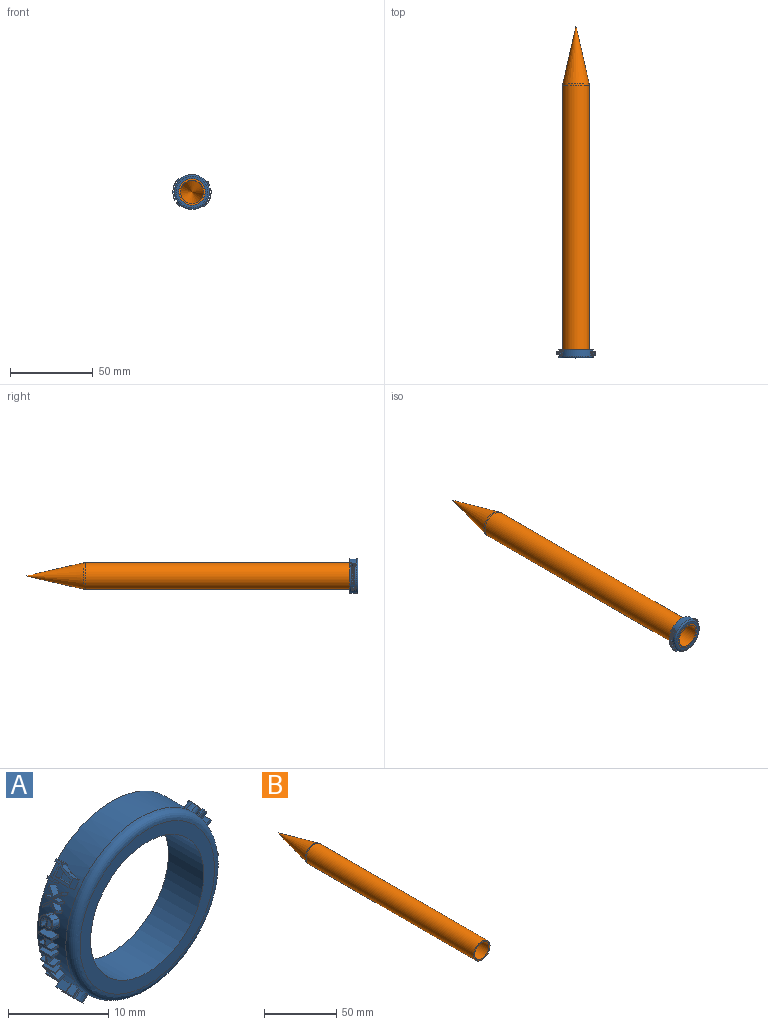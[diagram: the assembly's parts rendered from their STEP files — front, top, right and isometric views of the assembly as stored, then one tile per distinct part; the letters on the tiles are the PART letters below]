
ASSEMBLY  parts=2 mates=1
PART A: 312 faces, bbox 23x5x21 mm
  f0: plane 2.34x0.74mm, normal (0.74,0,0.67), area 2.3mm2, adj f1,f9,f10,f32
  f1: plane 0.93x0.87mm, normal (0,-1,0), area 0.3mm2, adj f0,f2,f10,f32
  f2: plane 2.36x0.74mm, normal (-0.74,0,-0.67), area 2.4mm2, adj f1,f3,f10,f32
  f3: extruded ~0.8x0.73mm, area 0.3mm2, adj f2,f4,f10,f32
  f4: extruded ~0.91x0.86mm, area 0.3mm2, adj f3,f5,f10,f32
  f5: extruded ~0.91x0.86mm, area 0.2mm2, adj f4,f6,f10,f32
  f6: plane 0.74x0.67mm, normal (-0.74,0,-0.67), area 0.2mm2, adj f5,f7,f10,f32
  f7: extruded ~0.91x0.86mm, area 0.2mm2, adj f6,f8,f10,f32
  f8: extruded ~1.05x1.01mm, area 0.5mm2, adj f7,f9,f10,f32
  f9: extruded ~0.85x0.79mm, area 0.5mm2, adj f0,f8,f10,f32
  f10: cylinder r=11.5mm len=2.98mm, axis (0,1,0), area 0.9mm2, adj f0,f1,f2,f3,f4,f5,f6,f7
  f11: extruded ~0.96x0.85mm, area 0.3mm2, adj f12,f24,f30,f32
  f12: extruded ~0.97x0.87mm, area 0.3mm2, adj f11,f13,f30,f32
  f13: extruded ~1.18x1.12mm, area 0.7mm2, adj f12,f14,f30,f32
  f14: extruded ~0.93x0.82mm, area 0.7mm2, adj f13,f15,f30,f32
  f15: extruded ~0.92x0.8mm, area 0.7mm2, adj f14,f16,f30,f32
  f16: extruded ~1.14x1.08mm, area 0.6mm2, adj f15,f17,f30,f32
  f17: extruded ~1.12x1.05mm, area 0.6mm2, adj f16,f18,f30,f32
  f18: extruded ~0.91x0.79mm, area 0.6mm2, adj f17,f19,f30,f32
  f19: plane 0.78x0.63mm, normal (0.63,0,0.78), area 0.2mm2, adj f18,f20,f30,f32
  f20: plane 1.59x1.53mm, normal (0,1,0), area 1.2mm2, adj f19,f21,f30,f32
  f21: extruded ~0.88x0.76mm, area 0.5mm2, adj f20,f22,f30,f32
  f22: extruded ~1.05x0.96mm, area 0.5mm2, adj f21,f23,f30,f32
  f23: extruded ~1.15x1.08mm, area 0.6mm2, adj f22,f24,f30,f32
  f24: plane 0.78x0.63mm, normal (0.63,0,0.78), area 0.2mm2, adj f11,f23,f30,f32
  f25: plane 1.36x1.35mm, normal (0,-1,0), area 0.9mm2, adj f26,f29,f30,f31
  f26: extruded ~0.88x0.75mm, area 0.4mm2, adj f25,f27,f30,f31
  f27: extruded ~0.99x0.9mm, area 0.4mm2, adj f26,f28,f30,f31
  f28: extruded ~0.98x0.88mm, area 0.4mm2, adj f27,f29,f30,f31
  f29: extruded ~0.85x0.72mm, area 0.4mm2, adj f25,f28,f30,f31
  f30: cylinder r=11.5mm len=1.83mm, axis (0,1,0), area 1.2mm2, adj f11,f12,f13,f14,f15,f16,f17,f18
  f31: cylinder r=10.5mm len=0.72mm, axis (0,1,0), area 0.4mm2, adj f25,f26,f27,f28,f29
  f32: cylinder r=10.5mm len=21mm, axis (0,1,0), area 238.7mm2, adj f0,f1,f2,f3,f4,f5,f6,f7
  f33: plane 1.21x0.88mm, normal (0.48,0,0.87), area 1.2mm2, adj f32,f34,f51,f60
  f34: plane 0.96x0.66mm, normal (0,1,0), area 0.2mm2, adj f32,f33,f35,f60
  f35: plane 0.9x0.53mm, normal (-0.47,0.21,-0.86), area 0.3mm2, adj f32,f34,f36,f60
  f36: plane 0.88x0.5mm, normal (0,1,0), area 0mm2, adj f32,f35,f37,f60
  f37: extruded ~1.01x0.72mm, area 0.4mm2, adj f32,f36,f38,f60
  f38: extruded ~1.03x0.77mm, area 0.3mm2, adj f32,f37,f39,f60
  f39: extruded ~1.09x0.85mm, area 0.4mm2, adj f32,f38,f40,f60
  f40: extruded ~0.96x0.62mm, area 0.4mm2, adj f32,f39,f41,f60
  f41: extruded ~1.31x1.25mm, area 1.2mm2, adj f32,f40,f42,f60
  f42: plane 1.01x0.75mm, normal (-0.02,-1,-0.03), area 0.3mm2, adj f32,f41,f43,f60
  f43: plane 0.88x0.49mm, normal (-0.48,0,-0.87), area 0.1mm2, adj f32,f42,f44,f60
  f44: extruded ~0.92x0.56mm, area 0.3mm2, adj f32,f43,f45,f60
  f45: extruded ~1.02x0.74mm, area 0.3mm2, adj f32,f44,f46,f60
  f46: extruded ~1.13x0.93mm, area 0.5mm2, adj f32,f45,f47,f60
  f47: plane 0.92x0.56mm, normal (-0.45,0.37,-0.81), area 0.2mm2, adj f32,f46,f48,f60
  f48: extruded ~1.02x0.74mm, area 0.3mm2, adj f32,f47,f49,f60
  f49: extruded ~1.03x0.76mm, area 0.3mm2, adj f32,f48,f50,f60
  f50: extruded ~1.11x0.9mm, area 0.5mm2, adj f32,f49,f51,f60
  f51: extruded ~0.96x0.62mm, area 0.5mm2, adj f32,f33,f50,f60
  f52: extruded ~0.95x0.61mm, area 0.3mm2, adj f53,f59,f60,f61
  f53: extruded ~1.1x0.89mm, area 0.5mm2, adj f52,f54,f60,f61
  f54: plane 1x0.72mm, normal (0.02,1,0.04), area 0.3mm2, adj f53,f55,f60,f61
  f55: plane 0.88x0.49mm, normal (-0.48,0,-0.87), area 0.2mm2, adj f54,f56,f60,f61
  f56: extruded ~0.95x0.61mm, area 0.4mm2, adj f55,f57,f60,f61
  f57: extruded ~1.07x0.83mm, area 0.4mm2, adj f56,f58,f60,f61
  f58: extruded ~1x0.7mm, area 0.3mm2, adj f57,f59,f60,f61
  f59: extruded ~0.92x0.56mm, area 0.2mm2, adj f52,f58,f60,f61
  f60: cylinder r=11.5mm len=1.83mm, axis (0,1,0), area 1.2mm2, adj f33,f34,f35,f36,f37,f38,f39,f40
  f61: cylinder r=10.5mm len=0.76mm, axis (0,1,0), area 0.4mm2, adj f52,f53,f54,f55,f56,f57,f58,f59
  f62: extruded ~1.01x0.49mm, area 0.5mm2, adj f32,f63,f78,f79
  f63: extruded ~1.12x0.78mm, area 0.5mm2, adj f32,f62,f64,f79
  f64: extruded ~1.05x0.63mm, area 0.3mm2, adj f32,f63,f65,f79
  f65: extruded ~1.03x0.54mm, area 0.3mm2, adj f32,f64,f66,f79
  f66: plane 0.95x0.33mm, normal (0,-1,0), area 0mm2, adj f32,f65,f67,f79
  f67: plane 0.96x0.36mm, normal (0.32,-0.18,0.93), area 0.2mm2, adj f32,f66,f68,f79
  f68: plane 1.03x0.52mm, normal (0,-1,0), area 0.2mm2, adj f32,f67,f69,f79
  f69: plane 1.77x0.95mm, normal (-0.32,0,-0.95), area 1.8mm2, adj f32,f68,f70,f79
  f70: plane 1.05x0.57mm, normal (0,1,0), area 0.3mm2, adj f32,f69,f71,f79
  f71: plane 0.95x0.93mm, normal (0.32,0,0.95), area 0.9mm2, adj f32,f70,f72,f79
  f72: extruded ~0.99x0.5mm, area 0.5mm2, adj f32,f71,f73,f79
  f73: extruded ~1.08x0.71mm, area 0.4mm2, adj f32,f72,f74,f79
  f74: extruded ~1.05x0.62mm, area 0.3mm2, adj f32,f73,f75,f79
  f75: extruded ~0.98x0.42mm, area 0.3mm2, adj f32,f74,f76,f79
  f76: plane 1.14x0.95mm, normal (-0.32,0,-0.95), area 1.1mm2, adj f32,f75,f77,f79
  f77: plane 1.02x0.58mm, normal (0,1,0), area 0.3mm2, adj f32,f76,f78,f79
  f78: plane 1.15x0.95mm, normal (0.32,0,0.95), area 1.2mm2, adj f32,f62,f77,f79
  f79: cylinder r=11.5mm len=1.8mm, axis (0,1,0), area 1.1mm2, adj f62,f63,f64,f65,f66,f67,f68,f69
  f80: extruded ~1.03x0.49mm, area 0.5mm2, adj f32,f81,f96,f97
  f81: extruded ~1.07x0.62mm, area 0.5mm2, adj f32,f80,f82,f97
  f82: extruded ~1.04x0.47mm, area 0.3mm2, adj f32,f81,f83,f97
  f83: extruded ~1.03x0.37mm, area 0.3mm2, adj f32,f82,f84,f97
  f84: plane 0.99x0.15mm, normal (0,-1,0), area 0mm2, adj f32,f83,f85,f97
  f85: plane 1x0.24mm, normal (0.14,-0.18,0.97), area 0.2mm2, adj f32,f84,f86,f97
  f86: plane 1.03x0.35mm, normal (0,-1,0), area 0.2mm2, adj f32,f85,f87,f97
  f87: plane 1.77x0.99mm, normal (-0.14,0,-0.99), area 1.8mm2, adj f32,f86,f88,f97
  f88: plane 1.04x0.4mm, normal (0,1,0), area 0.3mm2, adj f32,f87,f89,f97
  f89: plane 0.99x0.93mm, normal (0.14,0,0.99), area 0.9mm2, adj f32,f88,f90,f97
  f90: extruded ~1.01x0.5mm, area 0.5mm2, adj f32,f89,f91,f97
  f91: extruded ~1.05x0.54mm, area 0.4mm2, adj f32,f90,f92,f97
  f92: extruded ~1.04x0.45mm, area 0.3mm2, adj f32,f91,f93,f97
  f93: extruded ~1.01x0.32mm, area 0.3mm2, adj f32,f92,f94,f97
  f94: plane 1.14x0.99mm, normal (-0.14,0,-0.99), area 1.1mm2, adj f32,f93,f95,f97
  f95: plane 1.01x0.41mm, normal (0,1,0), area 0.3mm2, adj f32,f94,f96,f97
  f96: plane 1.15x0.99mm, normal (0.14,0,0.99), area 1.2mm2, adj f32,f80,f95,f97
  f97: cylinder r=11.5mm len=1.8mm, axis (0,1,0), area 1.1mm2, adj f80,f81,f82,f83,f84,f85,f86,f87
  f98: plane 1.77x1mm, normal (-0.01,0,-1), area 1.8mm2, adj f32,f99,f101,f102
  f99: plane 1x0.28mm, normal (0,1,0), area 0.3mm2, adj f32,f98,f100,f102
  f100: plane 1.77x1mm, normal (0.01,0,1), area 1.8mm2, adj f32,f99,f101,f102
  f101: plane 1x0.28mm, normal (0,-1,0), area 0.3mm2, adj f32,f98,f100,f102
  f102: cylinder r=11.5mm len=1.77mm, axis (0,1,0), area 0.5mm2, adj f98,f99,f100,f101
  f103: extruded ~1x0.12mm, area 0.1mm2, adj f32,f104,f110,f111
  f104: extruded ~1x0.13mm, area 0.1mm2, adj f32,f103,f105,f111
  f105: extruded ~1x0.13mm, area 0.1mm2, adj f32,f104,f106,f111
  f106: extruded ~1x0.12mm, area 0.1mm2, adj f32,f105,f107,f111
  f107: extruded ~1x0.12mm, area 0.1mm2, adj f32,f106,f108,f111
  f108: extruded ~1x0.13mm, area 0.1mm2, adj f32,f107,f109,f111
  f109: extruded ~1x0.13mm, area 0.1mm2, adj f32,f108,f110,f111
  f110: extruded ~1x0.12mm, area 0.1mm2, adj f32,f103,f109,f111
  f111: cylinder r=11.5mm len=0.36mm, axis (0,1,0), area 0.1mm2, adj f103,f104,f105,f106,f107,f108,f109,f110
  f112: extruded ~1.04x0.39mm, area 0.3mm2, adj f32,f113,f125,f131
  f113: extruded ~1.04x0.43mm, area 0.3mm2, adj f32,f112,f114,f131
  f114: extruded ~1.08x0.74mm, area 0.7mm2, adj f32,f113,f115,f131
  f115: extruded ~1.04x0.66mm, area 0.7mm2, adj f32,f114,f116,f131
  f116: extruded ~1.03x0.68mm, area 0.7mm2, adj f32,f115,f117,f131
  f117: extruded ~1.08x0.68mm, area 0.6mm2, adj f32,f116,f118,f131
  f118: extruded ~1.07x0.64mm, area 0.6mm2, adj f32,f117,f119,f131
  f119: extruded ~1.03x0.58mm, area 0.6mm2, adj f32,f118,f120,f131
  f120: plane 1x0.17mm, normal (-0.12,0,0.99), area 0.2mm2, adj f32,f119,f121,f131
  f121: plane 1.33x1.16mm, normal (0,1,0), area 1.2mm2, adj f32,f120,f122,f131
  f122: extruded ~1.02x0.47mm, area 0.5mm2, adj f32,f121,f123,f131
  f123: extruded ~1.05x0.54mm, area 0.5mm2, adj f32,f122,f124,f131
  f124: extruded ~1.08x0.68mm, area 0.6mm2, adj f32,f123,f125,f131
  f125: plane 0.99x0.24mm, normal (-0.12,0,0.99), area 0.2mm2, adj f32,f112,f124,f131
  f126: plane 1.1x1.04mm, normal (0,-1,0), area 0.9mm2, adj f127,f130,f131,f132
  f127: extruded ~1.02x0.38mm, area 0.4mm2, adj f126,f128,f131,f132
  f128: extruded ~1.04x0.46mm, area 0.4mm2, adj f127,f129,f131,f132
  f129: extruded ~1.04x0.44mm, area 0.4mm2, adj f128,f130,f131,f132
  f130: extruded ~1.01x0.39mm, area 0.4mm2, adj f126,f129,f131,f132
  f131: cylinder r=11.5mm len=1.83mm, axis (0,1,0), area 1.2mm2, adj f112,f113,f114,f115,f116,f117,f118,f119
  f132: cylinder r=10.5mm len=0.92mm, axis (0,1,0), area 0.4mm2, adj f126,f127,f128,f129,f130
  f133: plane 1.16x0.96mm, normal (0.23,-0.79,-0.57), area 0.8mm2, adj f32,f134,f141,f142
  f134: plane 0.98x0.51mm, normal (0.3,0.61,-0.73), area 0.2mm2, adj f32,f133,f135,f142
  f135: extruded ~1.07x0.73mm, area 0.5mm2, adj f32,f134,f136,f142
  f136: extruded ~0.96x0.45mm, area 0.1mm2, adj f32,f135,f137,f142
  f137: extruded ~0.93x0.4mm, area 0.4mm2, adj f32,f136,f138,f142
  f138: plane 1.68x0.93mm, normal (0.38,0,-0.93), area 1.7mm2, adj f32,f137,f139,f142
  f139: plane 1.03x0.62mm, normal (0,1,0), area 0.3mm2, adj f32,f138,f140,f142
  f140: plane 2.36x0.93mm, normal (-0.38,0,0.93), area 2.4mm2, adj f32,f139,f141,f142
  f141: plane 1.02x0.58mm, normal (0,-1,0), area 0.2mm2, adj f32,f133,f140,f142
  f142: cylinder r=11.5mm len=2.36mm, axis (0,1,0), area 0.8mm2, adj f133,f134,f135,f136,f137,f138,f139,f140
  f143: extruded ~1.17x1.02mm, area 0.7mm2, adj f32,f144,f157,f168
  f144: extruded ~0.98x0.77mm, area 0.8mm2, adj f32,f143,f145,f168
  f145: extruded ~1.04x1.01mm, area 1.1mm2, adj f32,f144,f146,f168
  f146: extruded ~1.28x1.21mm, area 0.9mm2, adj f32,f145,f147,f168
  f147: extruded ~1.02x0.77mm, area 0.3mm2, adj f32,f146,f148,f168
  f148: plane 0.86x0.52mm, normal (-0.52,0,0.86), area 0.2mm2, adj f32,f147,f149,f168
  f149: extruded ~1.01x0.77mm, area 0.3mm2, adj f32,f148,f150,f168
  f150: extruded ~1.16x1.01mm, area 0.6mm2, adj f32,f149,f151,f168
  f151: extruded ~0.98x0.74mm, area 0.8mm2, adj f32,f150,f152,f168
  f152: plane 0.87x0.53mm, normal (0,-1,0), area 0mm2, adj f32,f151,f153,f168
  f153: extruded ~1.16x1mm, area 0.7mm2, adj f32,f152,f154,f168
  f154: extruded ~1.13x0.95mm, area 0.6mm2, adj f32,f153,f155,f168
  f155: extruded ~0.96x0.68mm, area 0.6mm2, adj f32,f154,f156,f168
  f156: extruded ~0.97x0.7mm, area 0.6mm2, adj f32,f155,f157,f168
  f157: extruded ~1.15x0.99mm, area 0.6mm2, adj f32,f143,f156,f168
  f158: extruded ~0.89x0.57mm, area 0.3mm2, adj f159,f167,f168,f169
  f159: extruded ~0.9x0.58mm, area 0.2mm2, adj f158,f160,f168,f169
  f160: extruded ~0.96x0.69mm, area 0.3mm2, adj f159,f161,f168,f169
  f161: extruded ~1x0.75mm, area 0.3mm2, adj f160,f162,f168,f169
  f162: extruded ~1.04x0.82mm, area 0.4mm2, adj f161,f163,f168,f169
  f163: extruded ~0.92x0.62mm, area 0.4mm2, adj f162,f164,f168,f169
  f164: extruded ~0.93x0.63mm, area 0.4mm2, adj f163,f165,f168,f169
  f165: extruded ~1.05x0.82mm, area 0.4mm2, adj f164,f166,f168,f169
  f166: extruded ~1x0.75mm, area 0.3mm2, adj f165,f167,f168,f169
  f167: extruded ~0.96x0.68mm, area 0.3mm2, adj f158,f166,f168,f169
  f168: cylinder r=11.5mm len=2.43mm, axis (0,1,0), area 1.4mm2, adj f143,f144,f145,f146,f147,f148,f149,f150
  f169: cylinder r=10.5mm len=1.06mm, axis (0,1,0), area 0.8mm2, adj f158,f159,f160,f161,f162,f163,f164,f165
  f170: plane 0.96x0.86mm, normal (0,-1,0), area 0.3mm2, adj f32,f171,f182,f188
  f171: plane 0.86x0.8mm, normal (-0.61,0,-0.79), area 0.9mm2, adj f32,f170,f172,f188
  f172: plane 0.94x0.83mm, normal (0,1,0), area 0.3mm2, adj f32,f171,f173,f188
  f173: plane 0.8x0.62mm, normal (0.61,0,0.79), area 0.6mm2, adj f32,f172,f174,f188
  f174: plane 1.9x1.8mm, normal (0,1,0), area 1.6mm2, adj f32,f173,f175,f188
  f175: plane 0.8x0.62mm, normal (-0.61,0,-0.79), area 0.6mm2, adj f32,f174,f176,f188
  f176: plane 0.98x0.8mm, normal (0,1,0), area 0.3mm2, adj f32,f175,f177,f188
  f177: plane 0.86x0.8mm, normal (0.61,0,0.79), area 0.9mm2, adj f32,f176,f178,f188
  f178: plane 0.92x0.74mm, normal (0,-1,0), area 0.2mm2, adj f32,f177,f179,f188
  f179: extruded ~1.08x1.02mm, area 1.1mm2, adj f32,f178,f180,f188
  f180: extruded ~1.09x0.92mm, area 1.1mm2, adj f32,f179,f181,f188
  f181: plane 1.46x1.43mm, normal (0,-1,0), area 1.1mm2, adj f32,f180,f182,f188
  f182: plane 2.11x0.8mm, normal (-0.61,0,-0.79), area 2.1mm2, adj f32,f170,f181,f188
  f183: extruded ~0.94x0.92mm, area 1mm2, adj f184,f187,f188,f189
  f184: plane 1.12x1.04mm, normal (0,1,0), area 0.5mm2, adj f183,f185,f188,f189
  f185: plane 1.86x0.8mm, normal (0.61,0,0.79), area 1.9mm2, adj f184,f186,f188,f189
  f186: plane 1.49x1.49mm, normal (0,-1,0), area 1.1mm2, adj f185,f187,f188,f189
  f187: extruded ~1.05x0.93mm, area 1mm2, adj f183,f186,f188,f189
  f188: cylinder r=11.5mm len=2.97mm, axis (0,1,0), area 2.2mm2, adj f170,f171,f172,f173,f174,f175,f176,f177
  f189: cylinder r=10.5mm len=1.86mm, axis (0,1,0), area 1.5mm2, adj f183,f184,f185,f186,f187
  f190: plane 1.25x1.05mm, normal (-0.31,-0.65,-0.7), area 1.1mm2, adj f32,f191,f207,f208
  f191: plane 0.92x0.86mm, normal (0.4,0,0.92), area 0.9mm2, adj f32,f190,f192,f208
  f192: plane 1.02x0.63mm, normal (0,-1,0), area 0.2mm2, adj f32,f191,f193,f208
  f193: plane 0.92x0.86mm, normal (-0.4,0,-0.92), area 0.9mm2, adj f32,f192,f194,f208
  f194: plane 1.19x1.08mm, normal (0.3,-0.65,0.7), area 1.1mm2, adj f32,f193,f195,f208
  f195: plane 1.02x0.68mm, normal (0,-1,0), area 0.3mm2, adj f32,f194,f196,f208
  f196: plane 1.17x1.1mm, normal (-0.3,0.65,-0.69), area 1.1mm2, adj f32,f195,f197,f208
  f197: plane 1.19x1.16mm, normal (-0.3,-0.66,-0.69), area 1.2mm2, adj f32,f196,f198,f208
  f198: plane 1.02x0.7mm, normal (0,1,0), area 0.3mm2, adj f32,f197,f199,f208
  f199: plane 1.2x1.13mm, normal (0.3,0.66,0.69), area 1.2mm2, adj f32,f198,f200,f208
  f200: plane 0.92x0.9mm, normal (-0.4,0,-0.92), area 0.9mm2, adj f32,f199,f201,f208
  f201: plane 1.02x0.63mm, normal (0,1,0), area 0.2mm2, adj f32,f200,f202,f208
  f202: plane 0.92x0.9mm, normal (0.4,0,0.92), area 0.9mm2, adj f32,f201,f203,f208
  f203: plane 1.27x1.1mm, normal (-0.3,0.66,-0.69), area 1.2mm2, adj f32,f202,f204,f208
  f204: plane 1.07x0.67mm, normal (0,1,0), area 0.3mm2, adj f32,f203,f205,f208
  f205: plane 1.3x1.11mm, normal (0.3,-0.66,0.69), area 1.2mm2, adj f32,f204,f206,f208
  f206: plane 1.27x1.06mm, normal (0.3,0.65,0.69), area 1.1mm2, adj f32,f205,f207,f208
  f207: plane 1.07x0.66mm, normal (0,-1,0), area 0.3mm2, adj f32,f190,f206,f208
  f208: cylinder r=11.5mm len=2.21mm, axis (0,1,0), area 1.5mm2, adj f190,f191,f192,f193,f194,f195,f196,f197
  f209: extruded ~1.05x0.46mm, area 0.3mm2, adj f32,f210,f222,f228
  f210: extruded ~1.05x0.5mm, area 0.3mm2, adj f32,f209,f211,f228
  f211: extruded ~1.11x0.8mm, area 0.7mm2, adj f32,f210,f212,f228
  f212: extruded ~1.04x0.66mm, area 0.7mm2, adj f32,f211,f213,f228
  f213: extruded ~1.04x0.68mm, area 0.7mm2, adj f32,f212,f214,f228
  f214: extruded ~1.11x0.75mm, area 0.6mm2, adj f32,f213,f215,f228
  f215: extruded ~1.1x0.71mm, area 0.6mm2, adj f32,f214,f216,f228
  f216: extruded ~1.03x0.58mm, area 0.6mm2, adj f32,f215,f217,f228
  f217: plane 0.98x0.2mm, normal (-0.19,0,-0.98), area 0.2mm2, adj f32,f216,f218,f228
  f218: plane 1.39x1.21mm, normal (0,1,0), area 1.2mm2, adj f32,f217,f219,f228
  f219: extruded ~1.02x0.47mm, area 0.5mm2, adj f32,f218,f220,f228
  f220: extruded ~1.07x0.61mm, area 0.5mm2, adj f32,f219,f221,f228
  f221: extruded ~1.11x0.75mm, area 0.6mm2, adj f32,f220,f222,f228
  f222: plane 0.98x0.24mm, normal (-0.19,0,-0.98), area 0.2mm2, adj f32,f209,f221,f228
  f223: plane 1.16x1.1mm, normal (0,-1,0), area 0.9mm2, adj f224,f227,f228,f229
  f224: extruded ~1.02x0.38mm, area 0.4mm2, adj f223,f225,f228,f229
  f225: extruded ~1.05x0.53mm, area 0.4mm2, adj f224,f226,f228,f229
  f226: extruded ~1.05x0.51mm, area 0.4mm2, adj f225,f227,f228,f229
  f227: extruded ~1.01x0.39mm, area 0.4mm2, adj f223,f226,f228,f229
  f228: cylinder r=11.5mm len=1.83mm, axis (0,1,0), area 1.2mm2, adj f209,f210,f211,f212,f213,f214,f215,f216
  f229: cylinder r=10.5mm len=0.91mm, axis (0,1,0), area 0.4mm2, adj f223,f224,f225,f226,f227
  f230: plane 1.02x0.28mm, normal (0,1,0), area 0.3mm2, adj f32,f231,f241,f242
  f231: plane 1x0.8mm, normal (-0.01,0,-1), area 0.8mm2, adj f32,f230,f232,f242
  f232: plane 1.02x1mm, normal (0,1,0), area 1mm2, adj f32,f231,f233,f242
  f233: plane 1x0.8mm, normal (0.01,0,1), area 0.8mm2, adj f32,f232,f234,f242
  f234: plane 1.02x0.28mm, normal (0,1,0), area 0.3mm2, adj f32,f233,f235,f242
  f235: plane 1.77x1mm, normal (-0.01,0,-1), area 1.8mm2, adj f32,f234,f236,f242
  f236: plane 1.02x0.28mm, normal (0,-1,0), area 0.3mm2, adj f32,f235,f237,f242
  f237: plane 1x0.74mm, normal (0.01,0,1), area 0.7mm2, adj f32,f236,f238,f242
  f238: plane 1.02x1mm, normal (0,-1,0), area 1mm2, adj f32,f237,f239,f242
  f239: plane 1x0.74mm, normal (-0.01,0,-1), area 0.7mm2, adj f32,f238,f240,f242
  f240: plane 1.02x0.28mm, normal (0,-1,0), area 0.3mm2, adj f32,f239,f241,f242
  f241: plane 1.77x1mm, normal (0.01,0,1), area 1.8mm2, adj f32,f230,f240,f242
  f242: cylinder r=11.5mm len=1.77mm, axis (0,1,0), area 1.2mm2, adj f230,f231,f232,f233,f234,f235,f236,f237
  f243: plane 1.02x0.45mm, normal (0,1,0), area 0.3mm2, adj f32,f244,f254,f255
  f244: plane 0.98x0.8mm, normal (0.18,0,-0.98), area 0.8mm2, adj f32,f243,f245,f255
  f245: plane 1.17x1.16mm, normal (0,1,0), area 1mm2, adj f32,f244,f246,f255
  f246: plane 0.98x0.8mm, normal (-0.18,0,0.98), area 0.8mm2, adj f32,f245,f247,f255
  f247: plane 1.05x0.44mm, normal (0,1,0), area 0.3mm2, adj f32,f246,f248,f255
  f248: plane 1.77x0.99mm, normal (0.18,0,-0.98), area 1.8mm2, adj f32,f247,f249,f255
  f249: plane 1.05x0.44mm, normal (0,-1,0), area 0.3mm2, adj f32,f248,f250,f255
  f250: plane 0.98x0.74mm, normal (-0.18,0,0.98), area 0.7mm2, adj f32,f249,f251,f255
  f251: plane 1.17x1.16mm, normal (0,-1,0), area 1mm2, adj f32,f250,f252,f255
  f252: plane 0.98x0.74mm, normal (0.18,0,-0.98), area 0.7mm2, adj f32,f251,f253,f255
  f253: plane 1.02x0.45mm, normal (0,-1,0), area 0.3mm2, adj f32,f252,f254,f255
  f254: plane 1.77x0.99mm, normal (-0.18,0,0.98), area 1.8mm2, adj f32,f243,f253,f255
  f255: cylinder r=11.5mm len=1.77mm, axis (0,1,0), area 1.2mm2, adj f243,f244,f245,f246,f247,f248,f249,f250
  f256: plane 1.04x0.68mm, normal (0,1,0), area 0.3mm2, adj f32,f257,f269,f270
  f257: plane 1.5x1.29mm, normal (0.31,0.54,-0.79), area 1.8mm2, adj f32,f256,f258,f270
  f258: plane 0.94x0.38mm, normal (-0.37,-0.04,0.93), area 0.2mm2, adj f32,f257,f259,f270
  f259: plane 0.93x0.37mm, normal (-0.37,-0.02,0.93), area 0.2mm2, adj f32,f258,f260,f270
  f260: plane 1.08x0.93mm, normal (-0.37,0,0.93), area 1.1mm2, adj f32,f259,f261,f270
  f261: plane 1.04x0.59mm, normal (0,1,0), area 0.3mm2, adj f32,f260,f262,f270
  f262: plane 1.77x0.93mm, normal (0.37,0,-0.93), area 1.8mm2, adj f32,f261,f263,f270
  f263: plane 1.07x0.67mm, normal (0,-1,0), area 0.3mm2, adj f32,f262,f264,f270
  f264: plane 1.51x1.28mm, normal (-0.31,-0.54,0.79), area 1.8mm2, adj f32,f263,f265,f270
  f265: plane 0.93x0.37mm, normal (0.37,0.06,-0.93), area 0.1mm2, adj f32,f264,f266,f270
  f266: plane 0.94x0.38mm, normal (0.37,0.04,-0.93), area 0.3mm2, adj f32,f265,f267,f270
  f267: plane 1.12x0.93mm, normal (0.37,0,-0.93), area 1.1mm2, adj f32,f266,f268,f270
  f268: plane 1.01x0.61mm, normal (0,-1,0), area 0.3mm2, adj f32,f267,f269,f270
  f269: plane 1.77x0.93mm, normal (-0.37,0,0.93), area 1.8mm2, adj f32,f256,f268,f270
  f270: cylinder r=11.5mm len=1.77mm, axis (0,1,0), area 1.3mm2, adj f256,f257,f258,f259,f260,f261,f262,f263
  f271: plane 1.17x1.1mm, normal (-0.37,-0.79,0.49), area 0.8mm2, adj f32,f272,f279,f280
  f272: plane 0.88x0.72mm, normal (-0.48,0.61,0.63), area 0.2mm2, adj f32,f271,f273,f280
  f273: extruded ~1.03x0.91mm, area 0.5mm2, adj f32,f272,f274,f280
  f274: extruded ~0.85x0.66mm, area 0.1mm2, adj f32,f273,f275,f280
  f275: extruded ~0.81x0.61mm, area 0.4mm2, adj f32,f274,f276,f280
  f276: plane 1.68x0.8mm, normal (-0.6,0,0.8), area 1.7mm2, adj f32,f275,f277,f280
  f277: plane 0.96x0.81mm, normal (0,1,0), area 0.3mm2, adj f32,f276,f278,f280
  f278: plane 2.36x0.8mm, normal (0.6,0,-0.8), area 2.4mm2, adj f32,f277,f279,f280
  f279: plane 0.94x0.78mm, normal (0,-1,0), area 0.2mm2, adj f32,f271,f278,f280
  f280: cylinder r=11.5mm len=2.36mm, axis (0,1,0), area 0.8mm2, adj f271,f272,f273,f274,f275,f276,f277,f278
  f281: extruded ~1.13x1.12mm, area 0.7mm2, adj f32,f282,f295,f306
  f282: extruded ~0.88x0.86mm, area 0.8mm2, adj f32,f281,f283,f306
  f283: extruded ~1.04x0.92mm, area 1.1mm2, adj f32,f282,f284,f306
  f284: extruded ~1.28x1.28mm, area 0.9mm2, adj f32,f283,f285,f306
  f285: extruded ~0.93x0.91mm, area 0.3mm2, adj f32,f284,f286,f306
  f286: plane 0.72x0.7mm, normal (0.72,0,-0.69), area 0.2mm2, adj f32,f285,f287,f306
  f287: extruded ~0.93x0.91mm, area 0.3mm2, adj f32,f286,f288,f306
  f288: extruded ~1.12x1.11mm, area 0.6mm2, adj f32,f287,f289,f306
  f289: extruded ~0.88x0.86mm, area 0.8mm2, adj f32,f288,f290,f306
  f290: plane 0.73x0.71mm, normal (0,-1,0), area 0mm2, adj f32,f289,f291,f306
  f291: extruded ~1.12x1.11mm, area 0.7mm2, adj f32,f290,f292,f306
  f292: extruded ~1.08x1.07mm, area 0.6mm2, adj f32,f291,f293,f306
  f293: extruded ~0.86x0.83mm, area 0.6mm2, adj f32,f292,f294,f306
  f294: extruded ~0.87x0.85mm, area 0.6mm2, adj f32,f293,f295,f306
  f295: extruded ~1.11x1.1mm, area 0.6mm2, adj f32,f281,f294,f306
  f296: extruded ~0.77x0.74mm, area 0.3mm2, adj f297,f305,f306,f307
  f297: extruded ~0.77x0.75mm, area 0.2mm2, adj f296,f298,f306,f307
  f298: extruded ~0.86x0.84mm, area 0.3mm2, adj f297,f299,f306,f307
  f299: extruded ~0.91x0.89mm, area 0.3mm2, adj f298,f300,f306,f307
  f300: extruded ~0.97x0.95mm, area 0.4mm2, adj f299,f301,f306,f307
  f301: extruded ~0.81x0.78mm, area 0.4mm2, adj f300,f302,f306,f307
  f302: extruded ~0.81x0.79mm, area 0.4mm2, adj f301,f303,f306,f307
  f303: extruded ~0.97x0.95mm, area 0.4mm2, adj f302,f304,f306,f307
  f304: extruded ~0.91x0.89mm, area 0.3mm2, adj f303,f305,f306,f307
  f305: extruded ~0.85x0.83mm, area 0.3mm2, adj f296,f304,f306,f307
  f306: cylinder r=11.5mm len=2.43mm, axis (0,1,0), area 1.4mm2, adj f281,f282,f283,f284,f285,f286,f287,f288
  f307: cylinder r=10.5mm len=1.06mm, axis (0,1,0), area 0.8mm2, adj f296,f297,f298,f299,f300,f301,f302,f303
  f308: plane 19.01x19.01mm, normal (0,-1,0), area 82.5mm2, adj f310,f311
  f309: plane 21x21mm, normal (0,1,0), area 145.3mm2, adj f32,f310
  f310: cylinder r=8mm len=16mm, axis (0,1,0), area 251.3mm2, adj f308,f309
  f311: bspline ~20.99x20.98mm, area 103.8mm2, adj f32,f308
PART B: 8 faces, bbox 16x200x16 mm
  f0: cylinder r=7mm len=165mm, axis (0,1,0), area 7257.1mm2, adj f2,f4
  f1: cylinder r=8mm len=164.44mm, axis (0,1,0), area 8265.4mm2, adj f2,f5
  f2: plane 16x16mm, normal (0,-1,0), area 47.1mm2, adj f0,f1
  f3: cone r=8mm half-angle=12.9deg, axis (0,-1,0), area 874.2mm2, adj f5
  f4: plane 14x14mm, normal (0,-1,0), area 1.8mm2, adj f0,f6
  f5: torus R=3mm, axis (0,-1,0), area 56.2mm2, adj f1,f3
  f6: torus R=3mm, axis (0,-1,0), area 14.5mm2, adj f4,f7
  f7: cone r=7.03mm half-angle=12.9deg, axis (0,-1,0), area 671.1mm2, adj f6
PLACE A t=(10.49,76.55,101.96)mm fixed
PLACE B t=(10.49,236.55,101.96)mm
MATE fastened B.f0 <-> A.f310  axis (0,1,0) through (10.49,71.55,101.96)mm
